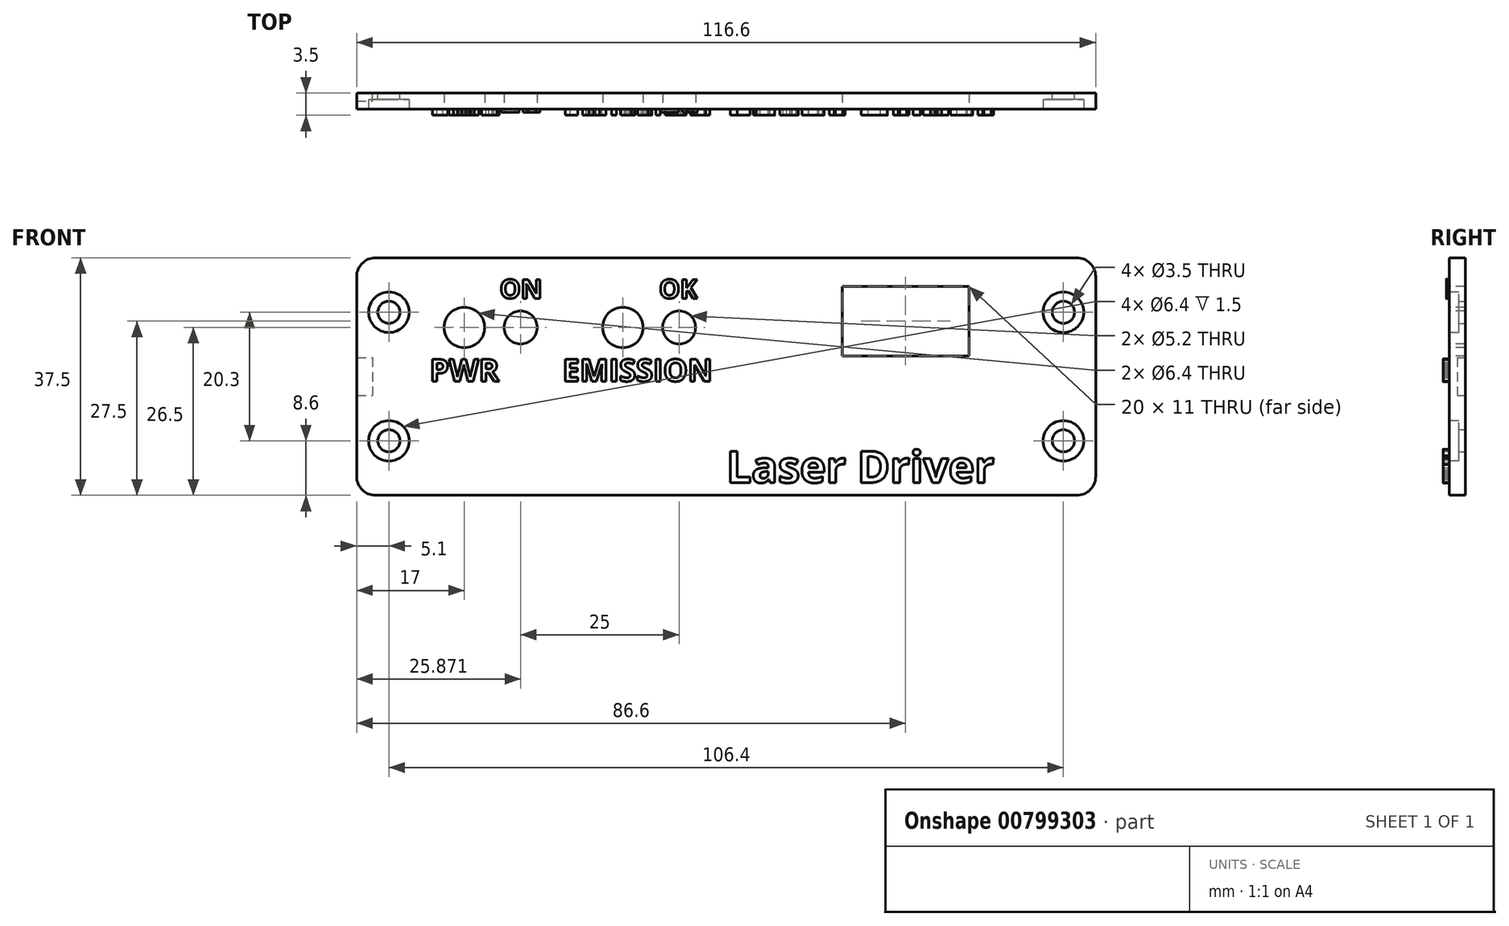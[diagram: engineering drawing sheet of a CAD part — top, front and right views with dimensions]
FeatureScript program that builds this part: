
annotation { "Feature Type Name" : "Feature", "Feature Type Description" : "" }
export const myFeature = defineFeature(function(context is Context, id is Id, definition is map)
    precondition{}
    {
        {
            var Q0;
            Q0=qCreatedBy(makeId("Front.planeOp"),FACE);
            var sketch = newSketch(context, id + "F0", { "sketchPlane" : qUnion([Q0])});
            skLineSegment(sketch, "E0.bottom", {"start": v(-55.3, 18.75) * mm, "end": v(55.3, 18.75) * mm});
            skLineSegment(sketch, "E0.top", {"start": v(-55.3, -18.75) * mm, "end": v(55.3, -18.75) * mm});
            skLineSegment(sketch, "E0.left", {"start": v(-58.3, 15.75) * mm, "end": v(-58.3, -15.75) * mm});
            skLineSegment(sketch, "E0.right", {"start": v(58.3, 15.75) * mm, "end": v(58.3, -15.75) * mm});
            skPoint(sketch, "E1.visualSharp", {"position": v(-58.3, 18.75) * mm});
            skArc(sketch, "E1.filletArc", {"start": v(-55.3, 18.75) * mm, "mid": v(-57.42, 17.87) * mm, "end": v(-58.3, 15.75) * mm});
            skPoint(sketch, "E2.visualSharp", {"position": v(58.3, 18.75) * mm});
            skArc(sketch, "E2.filletArc", {"start": v(58.3, 15.75) * mm, "mid": v(57.42, 17.87) * mm, "end": v(55.3, 18.75) * mm});
            skPoint(sketch, "E3.visualSharp", {"position": v(58.3, -18.75) * mm});
            skArc(sketch, "E3.filletArc", {"start": v(55.3, -18.75) * mm, "mid": v(57.42, -17.87) * mm, "end": v(58.3, -15.75) * mm});
            skPoint(sketch, "E4.visualSharp", {"position": v(-58.3, -18.75) * mm});
            skArc(sketch, "E4.filletArc", {"start": v(-58.3, -15.75) * mm, "mid": v(-57.42, -17.87) * mm, "end": v(-55.3, -18.75) * mm});
            skCircle(sketch, "E5", {"center": v(-53.2, 10.15) * mm, "radius": 1.75 * mm});
            skCircle(sketch, "E6", {"center": v(53.2, 10.15) * mm, "radius": 1.75 * mm});
            skCircle(sketch, "E7", {"center": v(-53.2, -10.15) * mm, "radius": 1.75 * mm});
            skCircle(sketch, "E8", {"center": v(53.2, -10.15) * mm, "radius": 1.75 * mm});
            skSolve(sketch);
        }
        {
            var Q0;
            Q0=makeQuery(id+"F0.imprint","IMPRINT",FACE,{"disambiguationData":[TD([[makeQuery(id+"F0.imprint","IMPRINT",EDGE,{"derivedFrom":sQuery(id+"F0.wireOp",EDGE,"E0.bottom")}),-1.0]])]});
            extrude(context, id + "F1", {"entities" : qUnion([Q0]), "depth" : 2.5 * mm});
        }
        {
            var Q0;
            Q0=makeQuery(id+"F1.opExtrude","CAP_FACE",FACE,{"disambiguationData":[OSD([sQuery(id+"F0.wireOp",EDGE,"E0.bottom"),sQuery(id+"F0.wireOp",EDGE,"E0.top"),sQuery(id+"F0.wireOp",EDGE,"E0.left"),sQuery(id+"F0.wireOp",EDGE,"E0.right"),sQuery(id+"F0.wireOp",EDGE,"E1.filletArc"),sQuery(id+"F0.wireOp",EDGE,"E2.filletArc"),sQuery(id+"F0.wireOp",EDGE,"E3.filletArc"),sQuery(id+"F0.wireOp",EDGE,"E4.filletArc"),sQuery(id+"F0.wireOp",EDGE,"E5"),sQuery(id+"F0.wireOp",EDGE,"E6"),sQuery(id+"F0.wireOp",EDGE,"E7"),sQuery(id+"F0.wireOp",EDGE,"E8")])],"isStart":false});
            var sketch = newSketch(context, id + "F2", { "sketchPlane" : qUnion([Q0])});
            skCircle(sketch, "E9", {"center": v(-53.2, 10.15) * mm, "radius": 3.2 * mm});
            skCircle(sketch, "E10", {"center": v(53.2, 10.15) * mm, "radius": 3.2 * mm});
            skCircle(sketch, "E11", {"center": v(-53.2, -10.15) * mm, "radius": 3.2 * mm});
            skCircle(sketch, "E12", {"center": v(53.2, -10.15) * mm, "radius": 3.2 * mm});
            skSolve(sketch);
        }
        {
            var Q0;
            Q0=qSketchRegion(id+"F2",true);
            extrude(context, id + "F3", {"entities" : qUnion([Q0]), "operationType" : NewBodyOperationType.REMOVE, "oppositeDirection" : true, "depth" : 1.5 * mm});
        }
        {
            var Q0;
            Q0=makeQuery(id+"F1.opExtrude","CAP_FACE",FACE,{"disambiguationData":[OSD([sQuery(id+"F0.wireOp",EDGE,"E0.bottom"),sQuery(id+"F0.wireOp",EDGE,"E0.top"),sQuery(id+"F0.wireOp",EDGE,"E0.left"),sQuery(id+"F0.wireOp",EDGE,"E0.right"),sQuery(id+"F0.wireOp",EDGE,"E1.filletArc"),sQuery(id+"F0.wireOp",EDGE,"E2.filletArc"),sQuery(id+"F0.wireOp",EDGE,"E3.filletArc"),sQuery(id+"F0.wireOp",EDGE,"E4.filletArc"),sQuery(id+"F0.wireOp",EDGE,"E5"),sQuery(id+"F0.wireOp",EDGE,"E6"),sQuery(id+"F0.wireOp",EDGE,"E7"),sQuery(id+"F0.wireOp",EDGE,"E8")])],"isStart":true});
            var sketch = newSketch(context, id + "F4", { "sketchPlane" : qUnion([Q0])});
            skLineSegment(sketch, "E13.bottom", {"start": v(58.3, 3) * mm, "end": v(55.8, 3) * mm});
            skLineSegment(sketch, "E13.top", {"start": v(58.3, -3) * mm, "end": v(55.8, -3) * mm});
            skLineSegment(sketch, "E13.left", {"start": v(58.3, 3) * mm, "end": v(58.3, -3) * mm});
            skLineSegment(sketch, "E13.right", {"start": v(55.8, 3) * mm, "end": v(55.8, -3) * mm});
            skSolve(sketch);
        }
        {
            var Q0;
            Q0=qSketchRegion(id+"F4",true);
            extrude(context, id + "F5", {"entities" : qUnion([Q0]), "operationType" : NewBodyOperationType.REMOVE, "oppositeDirection" : true, "depth" : 1.25 * mm});
        }
        {
            var Q0;
            Q0=makeQuery(id+"F1.opExtrude","CAP_FACE",FACE,{"disambiguationData":[OSD([sQuery(id+"F0.wireOp",EDGE,"E0.bottom"),sQuery(id+"F0.wireOp",EDGE,"E0.top"),sQuery(id+"F0.wireOp",EDGE,"E0.left"),sQuery(id+"F0.wireOp",EDGE,"E0.right"),sQuery(id+"F0.wireOp",EDGE,"E1.filletArc"),sQuery(id+"F0.wireOp",EDGE,"E2.filletArc"),sQuery(id+"F0.wireOp",EDGE,"E3.filletArc"),sQuery(id+"F0.wireOp",EDGE,"E4.filletArc"),sQuery(id+"F0.wireOp",EDGE,"E5"),sQuery(id+"F0.wireOp",EDGE,"E6"),sQuery(id+"F0.wireOp",EDGE,"E7"),sQuery(id+"F0.wireOp",EDGE,"E8")])],"isStart":false});
            var sketch = newSketch(context, id + "F6", { "sketchPlane" : qUnion([Q0])});
            skLineSegment(sketch, "E14", {"start": v(-63.46, 7.75) * mm, "end": v(64.15, 7.75) * mm, "construction": true});
            skLineSegment(sketch, "E15", {"start": v(-48.3, 18.75) * mm, "end": v(-48.3, -12.75) * mm, "construction": true});
            skLineSegment(sketch, "E16", {"start": v(48.3, -12.75) * mm, "end": v(48.3, 18.75) * mm, "construction": true});
            skLineSegment(sketch, "E17", {"start": v(-71.06, -1.55) * mm, "end": v(67.35, -1.55) * mm, "construction": true});
            skLineSegment(sketch, "E18", {"start": v(-32.43, 24.6) * mm, "end": v(-32.43, -13.66) * mm, "construction": true});
            skCircle(sketch, "E19", {"center": v(-41.3, 7.75) * mm, "radius": 3.2 * mm});
            skCircle(sketch, "E20", {"center": v(-32.43, 7.75) * mm, "radius": 2.6 * mm});
            skCircle(sketch, "E21.1.0.0", {"center": v(-16.3, 7.75) * mm, "radius": 3.2 * mm});
            skCircle(sketch, "E21.1.0.1", {"center": v(-7.43, 7.75) * mm, "radius": 2.6 * mm});
            skLineSegment(sketch, "E21.direction1", {"start": v(-41.3, 7.75) * mm, "end": v(-16.3, 7.75) * mm, "construction": true});
            skSolve(sketch);
        }
        {
            var Q0;
            Q0=qSketchRegion(id+"F6",true);
            extrude(context, id + "F7", {"entities" : qUnion([Q0]), "operationType" : NewBodyOperationType.REMOVE, "endBound" : BoundingType.THROUGH_ALL, "oppositeDirection" : true, "depth" : 25 * mm});
        }
        {
            var Q0;
            {var subQ237=sQuery(id+"F0.wireOp",EDGE,"E4.filletArc");var subQ240=sQuery(id+"F0.wireOp",EDGE,"E3.filletArc");var subQ244=sQuery(id+"F0.wireOp",EDGE,"E1.filletArc");var subQ247=sQuery(id+"F0.wireOp",EDGE,"E0.right");var subQ250=sQuery(id+"F0.wireOp",EDGE,"E0.left");var subQ306=sQuery(id+"F0.wireOp",EDGE,"E0.top");var subQ371=sQuery(id+"F0.wireOp",EDGE,"E0.bottom");var subQ372=makeQuery(id+"F1.opExtrude","SWEPT_FACE",FACE,{"disambiguationData":[OSD([subQ371])]});var subQ374=sQuery(id+"F0.wireOp",EDGE,"E2.filletArc");Q0=makeQuery(id+"F9eWGfNrq1sqSpY_1.boolean.opBoolean","SPLIT",FACE,{"disambiguationData":[TD([subQ372])],"derivedFrom":makeQuery(id+"F13.boolean.opBoolean","SPLIT",FACE,{"disambiguationData":[TD([subQ372])],"derivedFrom":makeQuery(id+"F11.boolean.opBoolean","SPLIT",FACE,{"disambiguationData":[TD([subQ372])],"derivedFrom":makeQuery(id+"F1.opExtrude","CAP_FACE",FACE,{"disambiguationData":[OSD([subQ371,subQ306,subQ250,subQ247,subQ244,subQ374,subQ240,subQ237,sQuery(id+"F0.wireOp",EDGE,"E5"),sQuery(id+"F0.wireOp",EDGE,"E6"),sQuery(id+"F0.wireOp",EDGE,"E7"),sQuery(id+"F0.wireOp",EDGE,"E8")])],"isStart":false})})})});}
            var sketch = newSketch(context, id + "F8", { "sketchPlane" : qUnion([Q0])});
            skLineSegment(sketch, "E22", {"start": v(28.3, 14.93) * mm, "end": v(28.3, 1.56) * mm, "construction": true});
            skLineSegment(sketch, "E23", {"start": v(8.8, 8.75) * mm, "end": v(44, 8.75) * mm, "construction": true});
            skLineSegment(sketch, "E24", {"start": v(28.3, 14.25) * mm, "end": v(18.3, 14.25) * mm});
            skLineSegment(sketch, "E25", {"start": v(18.3, 3.25) * mm, "end": v(28.3, 3.25) * mm});
            skLineSegment(sketch, "E26.MirrorCS", {"start": v(38.3, 3.25) * mm, "end": v(28.3, 3.25) * mm});
            skLineSegment(sketch, "E27.MirrorCS", {"start": v(28.3, 14.25) * mm, "end": v(38.3, 14.25) * mm});
            skLineSegment(sketch, "E28", {"start": v(18.3, 14.25) * mm, "end": v(18.3, 3.25) * mm});
            skLineSegment(sketch, "E29", {"start": v(38.3, 14.25) * mm, "end": v(38.3, 3.25) * mm});
            skSolve(sketch);
        }
        {
            var Q0;
            Q0=makeQuery(id+"F8.imprint","IMPRINT",FACE,{"disambiguationData":[TD([[makeQuery(id+"F8.imprint","IMPRINT",EDGE,{"derivedFrom":sQuery(id+"F8.wireOp",EDGE,"E24")}),1.0]])]});
            var Q1;
            Q1=makeQuery(id+"F8.imprint","IMPRINT",FACE,{"disambiguationData":[TD([[makeQuery(id+"F8.imprint","IMPRINT",EDGE,{"derivedFrom":sQuery(id+"F8.wireOp",EDGE,"Bv4UL4LP-5Ec1-gwm3-Mseu-Te5aNvBL9bas")}),1.0]])]});
            var Q2;
            Q2=makeQuery(id+"F8.imprint","IMPRINT",FACE,{"disambiguationData":[TD([[makeQuery(id+"F8.imprint","IMPRINT",EDGE,{"derivedFrom":sQuery(id+"F8.wireOp",EDGE,"a29f0001-43e5-4c7e-90f2-6ca24e596f3a2.MirrorC")}),-1.0]])]});
            extrude(context, id + "F9", {"entities" : qUnion([Q0, Q1, Q2]), "operationType" : NewBodyOperationType.REMOVE, "endBound" : BoundingType.THROUGH_ALL, "oppositeDirection" : true, "depth" : 25 * mm, "offsetDistance" : 25 * mm});
        }
        {
            var Q0;
            Q0=makeQuery(id+"F1.opExtrude","CAP_FACE",FACE,{"disambiguationData":[OSD([sQuery(id+"F0.wireOp",EDGE,"E0.bottom"),sQuery(id+"F0.wireOp",EDGE,"E0.top"),sQuery(id+"F0.wireOp",EDGE,"E0.left"),sQuery(id+"F0.wireOp",EDGE,"E0.right"),sQuery(id+"F0.wireOp",EDGE,"E1.filletArc"),sQuery(id+"F0.wireOp",EDGE,"E2.filletArc"),sQuery(id+"F0.wireOp",EDGE,"E3.filletArc"),sQuery(id+"F0.wireOp",EDGE,"E4.filletArc"),sQuery(id+"F0.wireOp",EDGE,"E5"),sQuery(id+"F0.wireOp",EDGE,"E6"),sQuery(id+"F0.wireOp",EDGE,"E7"),sQuery(id+"F0.wireOp",EDGE,"E8")])],"isStart":false});
            var sketch = newSketch(context, id + "F10", { "sketchPlane" : qUnion([Q0])});
            skText(sketch, "E30", { "text": "PWR", "fontName": "OpenSans-Bold.ttf"});
            skLineSegment(sketch, "E31", {"start": v(-40.46, -0.75) * mm, "end": v(129.06, -0.75) * mm, "construction": true});
            skLineSegment(sketch, "E32", {"start": v(-41.3, 7.75) * mm, "end": v(-41.3, 4.55) * mm, "construction": true});
            skLineSegment(sketch, "E33", {"start": v(28.3, 14.25) * mm, "end": v(28.3, 3.25) * mm, "construction": true});
            skText(sketch, "E34", { "text": "EMISSION", "fontName": "OpenSans-Bold.ttf"});
            const initialGuessF10  = {"E30": [-0.04678, -0.00075, 1, 0, 0.0035], "E34": [-0.02582, -0.00075, 1, 0, 0.0035]};
            skSetInitialGuess(sketch, initialGuessF10);
            skSolve(sketch);
        }
        {
            var Q0;
            Q0=qSketchRegion(id+"F10",true);
            extrude(context, id + "F11", {"entities" : qUnion([Q0]), "operationType" : NewBodyOperationType.ADD, "depth" : 1 * mm, "offsetDistance" : 25 * mm});
        }
        {
            var Q0;
            {var subQ70=sQuery(id+"F0.wireOp",EDGE,"E0.right");var subQ114=sQuery(id+"F0.wireOp",EDGE,"E3.filletArc");var subQ120=sQuery(id+"F0.wireOp",EDGE,"E4.filletArc");var subQ132=sQuery(id+"F0.wireOp",EDGE,"E1.filletArc");var subQ140=sQuery(id+"F0.wireOp",EDGE,"E0.top");var subQ143=sQuery(id+"F0.wireOp",EDGE,"E0.left");var subQ152=sQuery(id+"F0.wireOp",EDGE,"E2.filletArc");var subQ182=sQuery(id+"F0.wireOp",EDGE,"E0.bottom");var subQ183=makeQuery(id+"F1.opExtrude","SWEPT_FACE",FACE,{"disambiguationData":[OSD([subQ182])]});Q0=makeQuery(id+"Fu2jKsRN7ARvOCH_1.boolean.opBoolean","SPLIT",FACE,{"disambiguationData":[TD([subQ183])],"derivedFrom":makeQuery(id+"F11.boolean.opBoolean","SPLIT",FACE,{"disambiguationData":[TD([subQ183])],"derivedFrom":makeQuery(id+"F1.opExtrude","CAP_FACE",FACE,{"disambiguationData":[OSD([subQ182,subQ140,subQ143,subQ70,subQ132,subQ152,subQ114,subQ120,sQuery(id+"F0.wireOp",EDGE,"E5"),sQuery(id+"F0.wireOp",EDGE,"E6"),sQuery(id+"F0.wireOp",EDGE,"E7"),sQuery(id+"F0.wireOp",EDGE,"E8")])],"isStart":false})})});}
            var sketch = newSketch(context, id + "F12", { "sketchPlane" : qUnion([Q0])});
            skText(sketch, "E35", { "text": "Laser Driver", "fontName": "OpenSans-Bold.ttf"});
            const initialGuessF12  = {"E35": [6e-05, -0.01675, 1, 0, 0.005]};
            skSetInitialGuess(sketch, initialGuessF12);
            skSolve(sketch);
        }
        {
            var Q0;
            Q0=qSketchRegion(id+"F12",true);
            extrude(context, id + "F13", {"entities" : qUnion([Q0]), "operationType" : NewBodyOperationType.ADD, "depth" : 1 * mm});
        }
        {
            var Q0;
            {var subQ102=sQuery(id+"F0.wireOp",EDGE,"E0.bottom");var subQ103=makeQuery(id+"F1.opExtrude","SWEPT_FACE",FACE,{"disambiguationData":[OSD([subQ102])]});var subQ126=sQuery(id+"F0.wireOp",EDGE,"E0.top");var subQ129=sQuery(id+"F0.wireOp",EDGE,"E0.left");var subQ132=sQuery(id+"F0.wireOp",EDGE,"E0.right");var subQ135=sQuery(id+"F0.wireOp",EDGE,"E1.filletArc");var subQ138=sQuery(id+"F0.wireOp",EDGE,"E2.filletArc");var subQ141=sQuery(id+"F0.wireOp",EDGE,"E3.filletArc");var subQ144=sQuery(id+"F0.wireOp",EDGE,"E4.filletArc");Q0=makeQuery(id+"F13.boolean.opBoolean","SPLIT",FACE,{"disambiguationData":[TD([subQ103])],"derivedFrom":makeQuery(id+"F11.boolean.opBoolean","SPLIT",FACE,{"disambiguationData":[TD([subQ103])],"derivedFrom":makeQuery(id+"F1.opExtrude","CAP_FACE",FACE,{"disambiguationData":[OSD([subQ102,subQ126,subQ129,subQ132,subQ135,subQ138,subQ141,subQ144,sQuery(id+"F0.wireOp",EDGE,"E5"),sQuery(id+"F0.wireOp",EDGE,"E6"),sQuery(id+"F0.wireOp",EDGE,"E7"),sQuery(id+"F0.wireOp",EDGE,"E8")])],"isStart":false})})});}
            var sketch = newSketch(context, id + "F14", { "sketchPlane" : qUnion([Q0])});
            skLineSegment(sketch, "E36", {"start": v(-51.24, 12.35) * mm, "end": v(0, 12.35) * mm, "construction": true});
            skLineSegment(sketch, "E37", {"start": v(-32.43, 7.75) * mm, "end": v(-32.43, 10.35) * mm, "construction": true});
            skLineSegment(sketch, "E38", {"start": v(-7.43, 7.75) * mm, "end": v(-7.43, 10.35) * mm, "construction": true});
            skText(sketch, "E39", { "text": "ON", "fontName": "OpenSans-Bold.ttf"});
            skText(sketch, "E40", { "text": "OK", "fontName": "OpenSans-Bold.ttf"});
            const initialGuessF14  = {"E39": [-0.03573, 0.01235, 1, 0, 0.003], "E40": [-0.0106, 0.01235, 1, 0, 0.003]};
            skSetInitialGuess(sketch, initialGuessF14);
            skSolve(sketch);
        }
        {
            var Q0;
            Q0 = qSketchRegion(id + "F14", true);
            extrude(context, id + "F15", {"entities" : qUnion([Q0]), "operationType" : NewBodyOperationType.ADD, "depth" : 0.5 * mm, "offsetDistance" : 25 * mm});
        }
    });
